# Revit family: 1_Upper Cabinet-Double Door-Wall
name_source: partatom
category: Casework
revit_build: Autodesk Revit Architecture 2013 (Build: 20121003_2115(x64)
units: mm (PartAtom-declared; Revit-internal decimal feet)

## types (18) — shared parameters
Assembly Code = C1030410
Cabinet Material = <By Category>
Door/Drawer Material = <By Category>
Handle Material = Cabinets - Handles
Top Of Cabinet = 7' - 0"

## per-type parameters (varying)
| type | Depth | Height | Width |
| 36" | 1' - 0" | 2' - 6" | 3' - 0 1/32" |
| 48" | 1' - 0" | 2' - 6" | 4' - 0" |
| 36"/915mm 1'2H wall cab w/shelf | 1' - 0" | 1' - 2" | 3' - 0 1/32" |
| 33" 2 | 1' - 0" | 2' - 6" | 2' - 9 1/16" |
| 30" 2 | 1' - 0" | 2' - 6" | 2' - 6" |
| 24"/915mm 1'2H wall cab 2 | 1' - 0" | 1' - 2" | 2' - 0 3/8" |
| 36"/915mm 1'2H wall cab | 1' - 0" | 1' - 2" | 3' - 0 1/32" |
| 191 | 1' - 0" | 2' - 6" | 15' - 11" |
| 147 | 1' - 0" | 2' - 6" | 12' - 3" |
| 54" | 1' - 0" | 2' - 6" | 4' - 6" |
| 60" | 1' - 0" | 2' - 6" | 5' - 0" |
| 34" 1'2H 3 | 1' - 0" | 1' - 2" | 3' - 2" |
| 5182 | 1' - 0" | 2' - 6" | 17' - 0 1/32" |
| 2311 | 1' - 0" | 2' - 6" | 7' - 6 31/32" |
| 6045 | 1' - 2 1/32" | 2' - 6" | 19' - 10" |
| 43" | 1' - 0" | 2' - 6" | 3' - 7" |
| 18" | 1' - 0" | 2' - 6" | 1' - 6" |
| 36" 1'2H 2 | 1' - 0" | 1' - 2" | 3' - 4" |

## geometry (parser evidence)
native form markers: Sweep x2
no freeform markers — native parametric forms only
